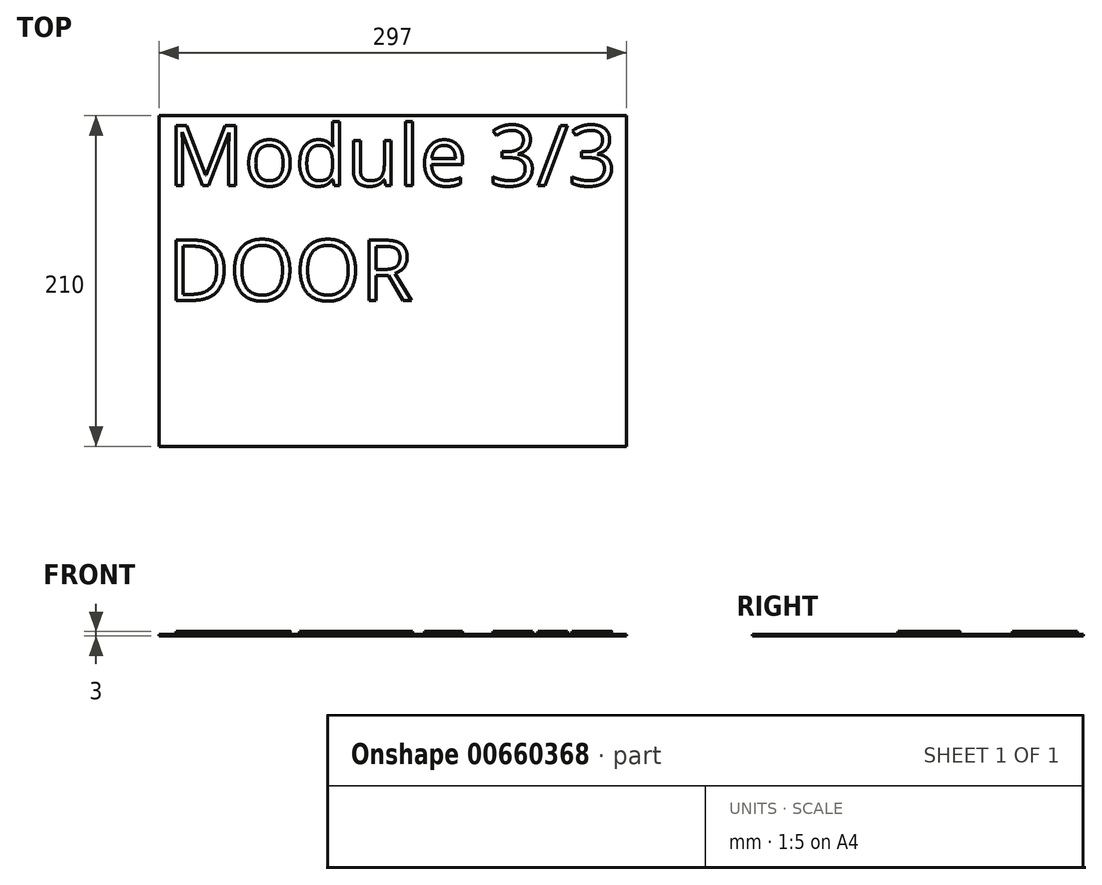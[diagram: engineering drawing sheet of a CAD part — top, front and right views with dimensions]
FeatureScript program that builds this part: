
annotation { "Feature Type Name" : "Feature", "Feature Type Description" : "" }
export const myFeature = defineFeature(function(context is Context, id is Id, definition is map)
    precondition{}
    {
        {
            var Q0;
            Q0=qCreatedBy(makeId("Top.planeOp"),FACE);
            var sketch = newSketch(context, id + "F0", { "sketchPlane" : qUnion([Q0])});
            skLineSegment(sketch, "E0.bottom", {"start": v(-195.9, 139.38) * mm, "end": v(101.1, 139.38) * mm});
            skLineSegment(sketch, "E0.top", {"start": v(-195.9, -70.62) * mm, "end": v(101.1, -70.62) * mm});
            skLineSegment(sketch, "E0.left", {"start": v(-195.9, 139.38) * mm, "end": v(-195.9, -70.62) * mm});
            skLineSegment(sketch, "E0.right", {"start": v(101.1, 139.38) * mm, "end": v(101.1, -70.62) * mm});
            skSolve(sketch);
        }
        {
            var Q0;
            Q0=qSketchRegion(id+"F0",true);
            extrude(context, id + "F1", {"entities" : qUnion([Q0]), "depth" : 1 * mm, "offsetDistance" : 25 * mm});
        }
        {
            var Q0;
            Q0=makeQuery(id+"F1.opExtrude","CAP_FACE",FACE,{"disambiguationData":[OSD([sQuery(id+"F0.wireOp",EDGE,"E0.bottom"),sQuery(id+"F0.wireOp",EDGE,"E0.top"),sQuery(id+"F0.wireOp",EDGE,"E0.left"),sQuery(id+"F0.wireOp",EDGE,"E0.right")])],"isStart":false});
            var sketch = newSketch(context, id + "F2", { "sketchPlane" : qUnion([Q0])});
            skText(sketch, "E1", { "text": "Module 3/3\nDOOR", "fontName": "OpenSans-Regular.ttf"});
            const initialGuessF2  = {"E1": [-0.19035, 0.095, 1, 0, 0.03858]};
            skSetInitialGuess(sketch, initialGuessF2);
            skSolve(sketch);
        }
        {
            var Q0;
            Q0=qSketchRegion(id+"F2",true);
            extrude(context, id + "F3", {"entities" : qUnion([Q0]), "operationType" : NewBodyOperationType.ADD, "depth" : 2 * mm, "offsetDistance" : 25 * mm});
        }
    });
